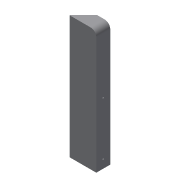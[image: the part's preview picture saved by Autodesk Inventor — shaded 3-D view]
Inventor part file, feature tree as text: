
AUTODESK INVENTOR PART (.ipt)
format: ipt  version: 2015 (Build 190159000, 159)  size: 91,648 bytes
history: native  units: mm
features: extrude x2, sketch x2, fillet x1, chamfer x1
ambient origin geometry x8: Origin, YZ Plane, XZ Plane, XY Plane, X Axis, Y Axis, Z Axis, Center Point
bodies: Solid1 (feature_tree)
feature tree (6):
  extrude  "Extrusion1"  Depth=88.0mm
  fillet  "Fillet1"  Radius=10.0mm
  chamfer  "Chamfer1"  Distance=2.0mm Angle=45.0deg
  extrude  "Extrusion2"  Depth=2.0mm
  sketch  "Sketch1"  dims[d0=19.0mm d1=88.0mm d2=10.0mm d3=0.0mm]
  sketch  "Sketch2"  dims[d4=4.0mm d5=9.5mm d6=2.0mm d7=45.0deg d8=50.0mm d9=5.0mm d10=38.0mm d11=1.0mm d12=1.0mm d13=1.0mm d14=2.0mm d15=0.0mm]
